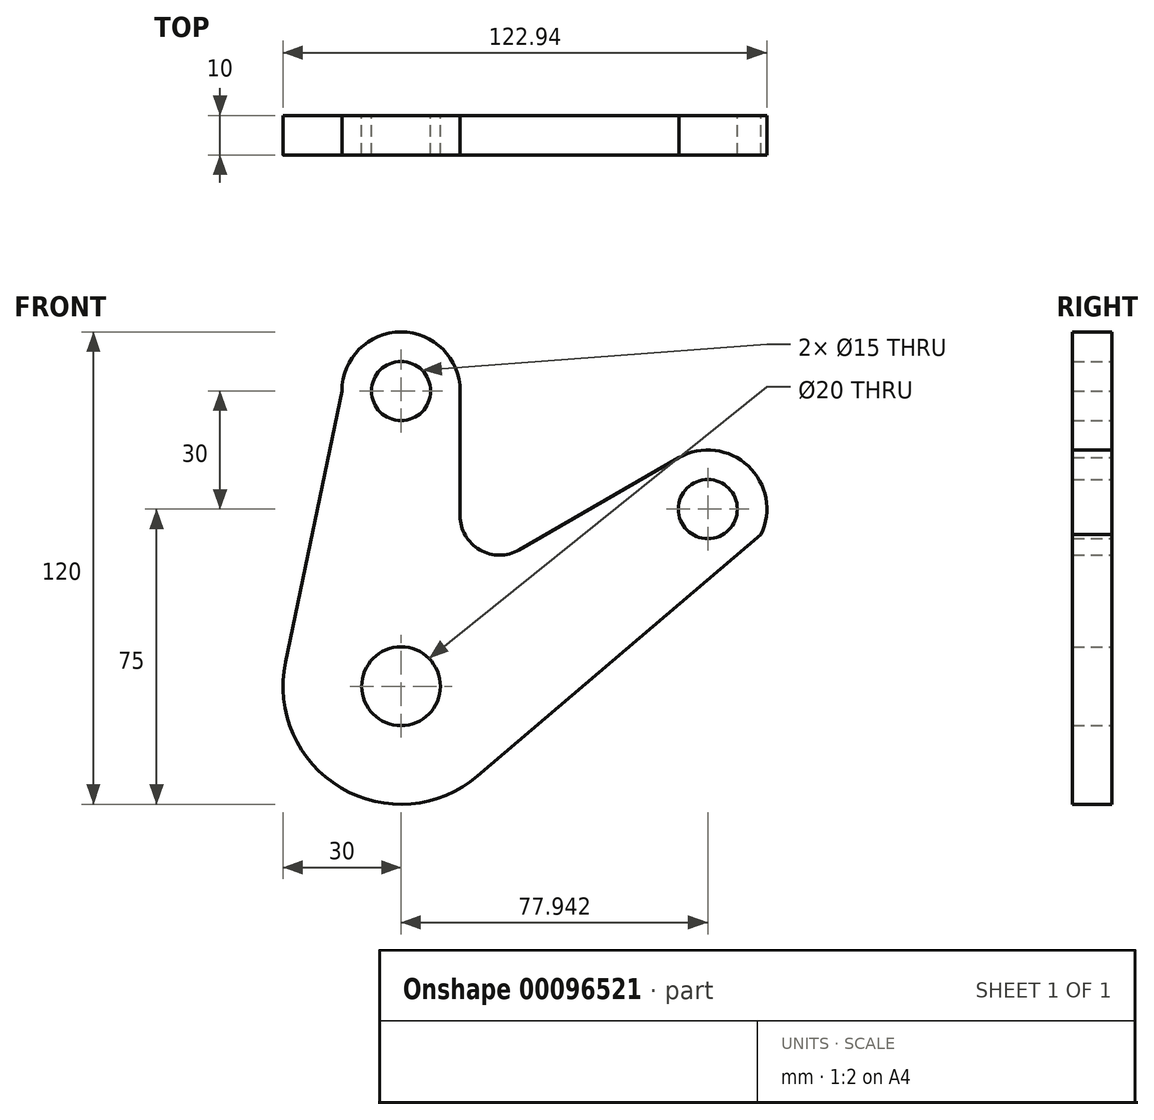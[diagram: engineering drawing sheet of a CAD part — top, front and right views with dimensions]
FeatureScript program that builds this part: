
annotation { "Feature Type Name" : "Feature", "Feature Type Description" : "" }
export const myFeature = defineFeature(function(context is Context, id is Id, definition is map)
    precondition{}
    {
        {
            var Q0;
            Q0=qCreatedBy(makeId("Front.planeOp"),FACE);
            var sketch = newSketch(context, id + "F0", { "sketchPlane" : qUnion([Q0])});
            skCircle(sketch, "E0", {"center": v(0, 0) * mm, "radius": 10 * mm});
            skArc(sketch, "E1", {"start": v(19.46, -22.83) * mm, "mid": v(-15.3, -25.8) * mm, "end": v(-29.37, 6.13) * mm});
            skCircle(sketch, "E2", {"center": v(0, 75) * mm, "radius": 7.5 * mm});
            skCircle(sketch, "E3", {"center": v(77.94, 45) * mm, "radius": 7.5 * mm});
            skLineSegment(sketch, "E4", {"start": v(0, 0) * mm, "end": v(77.94, 45) * mm, "construction": true});
            skLineSegment(sketch, "E5", {"start": v(0, 75) * mm, "end": v(0, 0) * mm, "construction": true});
            skLineSegment(sketch, "E6", {"start": v(-29.37, 6.13) * mm, "end": v(-15, 75) * mm});
            skArc(sketch, "E7", {"start": v(15, 75) * mm, "mid": v(0, 90) * mm, "end": v(-15, 75) * mm});
            skLineSegment(sketch, "E8", {"start": v(15, 75) * mm, "end": v(15, 43.3) * mm});
            skLineSegment(sketch, "E9", {"start": v(30, 34.64) * mm, "end": v(70.61, 58.09) * mm});
            skArc(sketch, "E10.filletArc", {"start": v(15, 43.3) * mm, "mid": v(20, 34.64) * mm, "end": v(30, 34.64) * mm});
            skLineSegment(sketch, "E11", {"start": v(19.46, -22.83) * mm, "end": v(91.47, 38.53) * mm});
            skArc(sketch, "E12", {"start": v(91.47, 38.53) * mm, "mid": v(88.2, 55.94) * mm, "end": v(70.61, 58.09) * mm});
            skSolve(sketch);
        }
        {
            var Q0;
            Q0 = qSketchRegion(id + "F0", true);
            extrude(context, id + "F1", {"entities" : qUnion([Q0]), "depth" : 10 * mm});
        }
    });
